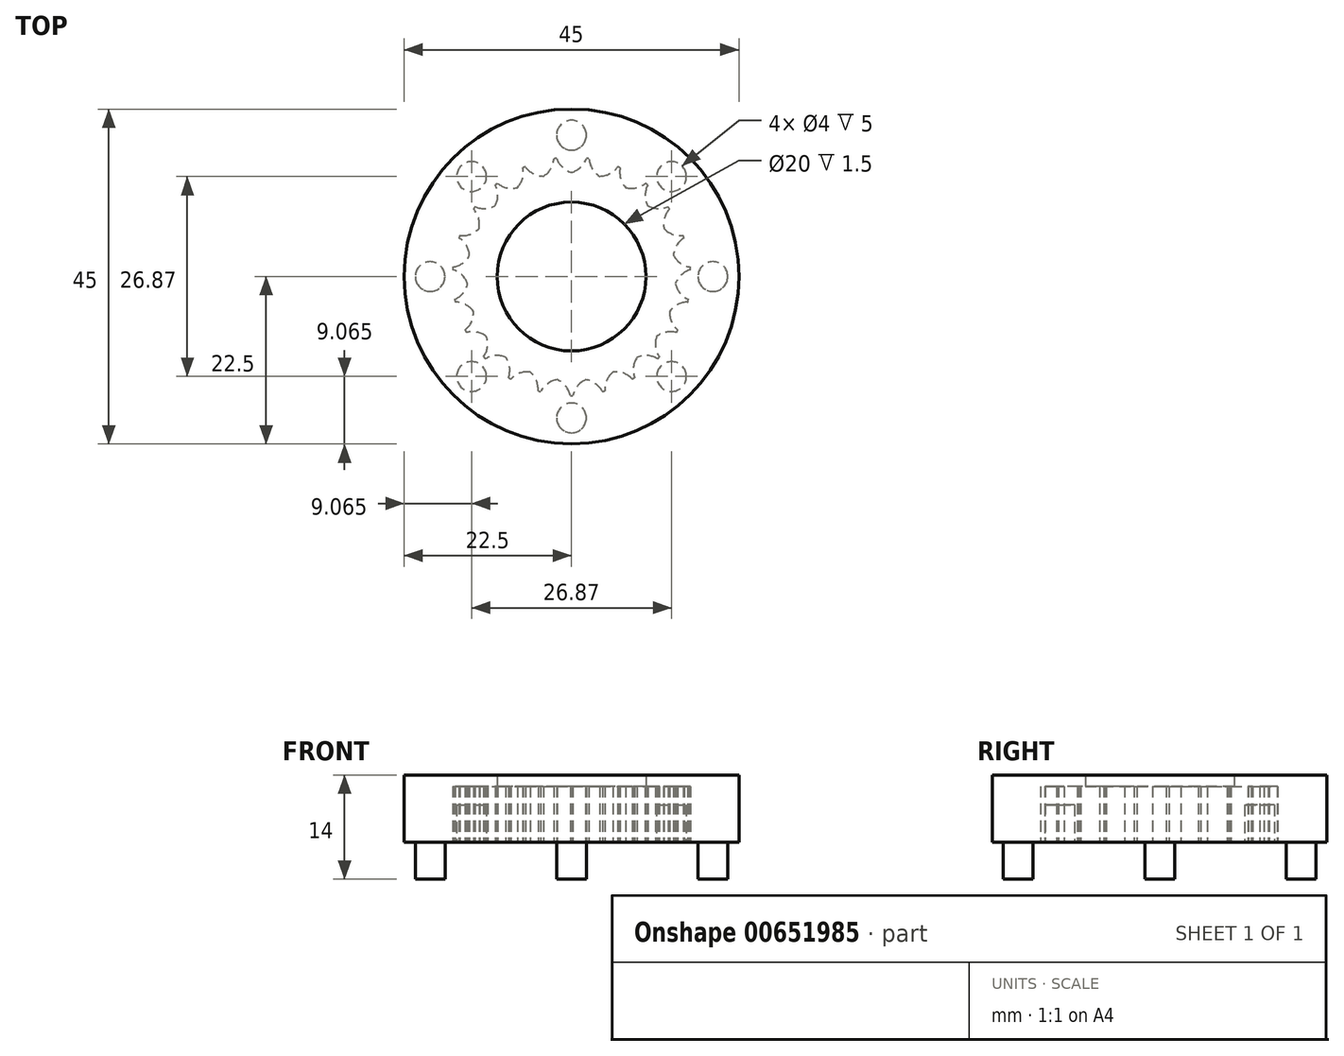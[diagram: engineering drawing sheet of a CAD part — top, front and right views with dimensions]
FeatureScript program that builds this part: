
annotation { "Feature Type Name" : "Feature", "Feature Type Description" : "" }
export const myFeature = defineFeature(function(context is Context, id is Id, definition is map)
    precondition{}
    {
        {
            var Q0;
            Q0=qCreatedBy(makeId("Top.planeOp"),FACE);
            var sketch = newSketch(context, id + "F0", { "sketchPlane" : qUnion([Q0])});
            skCircle(sketch, "E0", {"center": v(0, 0) * mm, "radius": 16 * mm});
            skCircle(sketch, "E1", {"center": v(0, 0) * mm, "radius": 22.5 * mm});
            skArc(sketch, "E2", {"start": v(-2, 15.87) * mm, "mid": v(-1.23, 14.7) * mm, "end": v(0, 14) * mm});
            skArc(sketch, "E3", {"start": v(0, 14) * mm, "mid": v(1.23, 14.7) * mm, "end": v(2, 15.87) * mm});
            skArc(sketch, "E4.1.0", {"start": v(-6.2, 14.75) * mm, "mid": v(-5.15, 13.82) * mm, "end": v(-3.78, 13.48) * mm});
            skArc(sketch, "E4.1.1", {"start": v(-3.78, 13.48) * mm, "mid": v(-2.78, 14.48) * mm, "end": v(-2.36, 15.83) * mm});
            skArc(sketch, "E4.2.0", {"start": v(-9.96, 12.52) * mm, "mid": v(-8.68, 11.92) * mm, "end": v(-7.27, 11.96) * mm});
            skArc(sketch, "E4.2.1", {"start": v(-7.27, 11.96) * mm, "mid": v(-6.59, 13.2) * mm, "end": v(-6.54, 14.6) * mm});
            skArc(sketch, "E4.3.0", {"start": v(-12.97, 9.37) * mm, "mid": v(-11.58, 9.13) * mm, "end": v(-10.23, 9.56) * mm});
            skArc(sketch, "E4.3.1", {"start": v(-10.23, 9.56) * mm, "mid": v(-9.9, 10.93) * mm, "end": v(-10.24, 12.3) * mm});
            skArc(sketch, "E4.4.0", {"start": v(-15.01, 5.53) * mm, "mid": v(-13.61, 5.67) * mm, "end": v(-12.43, 6.44) * mm});
            skArc(sketch, "E4.4.1", {"start": v(-12.43, 6.44) * mm, "mid": v(-12.48, 7.85) * mm, "end": v(-13.17, 9.08) * mm});
            skArc(sketch, "E4.5.0", {"start": v(-15.95, 1.27) * mm, "mid": v(-14.64, 1.79) * mm, "end": v(-13.7, 2.85) * mm});
            skArc(sketch, "E4.5.1", {"start": v(-13.7, 2.85) * mm, "mid": v(-14.14, 4.2) * mm, "end": v(-15.14, 5.19) * mm});
            skArc(sketch, "E4.6.0", {"start": v(-15.7, -3.08) * mm, "mid": v(-14.58, -2.23) * mm, "end": v(-13.97, -0.96) * mm});
            skArc(sketch, "E4.6.1", {"start": v(-13.97, -0.96) * mm, "mid": v(-14.74, 0.22) * mm, "end": v(-15.97, 0.91) * mm});
            skArc(sketch, "E4.7.0", {"start": v(-14.29, -7.2) * mm, "mid": v(-13.44, -6.08) * mm, "end": v(-13.2, -4.69) * mm});
            skArc(sketch, "E4.7.1", {"start": v(-13.2, -4.69) * mm, "mid": v(-14.26, -3.77) * mm, "end": v(-15.63, -3.43) * mm});
            skArc(sketch, "E4.8.0", {"start": v(-11.82, -10.79) * mm, "mid": v(-11.3, -9.48) * mm, "end": v(-11.44, -8.07) * mm});
            skArc(sketch, "E4.8.1", {"start": v(-11.44, -8.07) * mm, "mid": v(-12.71, -7.47) * mm, "end": v(-14.12, -7.52) * mm});
            skArc(sketch, "E4.9.0", {"start": v(-8.47, -13.58) * mm, "mid": v(-8.32, -12.17) * mm, "end": v(-8.84, -10.86) * mm});
            skArc(sketch, "E4.9.1", {"start": v(-8.84, -10.86) * mm, "mid": v(-10.23, -10.63) * mm, "end": v(-11.57, -11.05) * mm});
            skArc(sketch, "E4.10.0", {"start": v(-4.49, -15.36) * mm, "mid": v(-4.73, -13.97) * mm, "end": v(-5.58, -12.84) * mm});
            skArc(sketch, "E4.10.1", {"start": v(-5.58, -12.84) * mm, "mid": v(-6.98, -13) * mm, "end": v(-8.16, -13.76) * mm});
            skArc(sketch, "E4.11.0", {"start": v(-0.18, -16) * mm, "mid": v(-0.79, -14.73) * mm, "end": v(-1.9, -13.87) * mm});
            skArc(sketch, "E4.11.1", {"start": v(-1.9, -13.87) * mm, "mid": v(-3.22, -14.4) * mm, "end": v(-4.14, -15.45) * mm});
            skArc(sketch, "E4.12.0", {"start": v(4.14, -15.45) * mm, "mid": v(3.22, -14.4) * mm, "end": v(1.9, -13.87) * mm});
            skArc(sketch, "E4.12.1", {"start": v(1.9, -13.87) * mm, "mid": v(0.79, -14.73) * mm, "end": v(0.18, -16) * mm});
            skArc(sketch, "E4.13.0", {"start": v(8.16, -13.76) * mm, "mid": v(6.98, -13) * mm, "end": v(5.58, -12.84) * mm});
            skArc(sketch, "E4.13.1", {"start": v(5.58, -12.84) * mm, "mid": v(4.73, -13.97) * mm, "end": v(4.49, -15.36) * mm});
            skArc(sketch, "E4.14.0", {"start": v(11.57, -11.05) * mm, "mid": v(10.23, -10.63) * mm, "end": v(8.84, -10.86) * mm});
            skArc(sketch, "E4.14.1", {"start": v(8.84, -10.86) * mm, "mid": v(8.32, -12.17) * mm, "end": v(8.47, -13.58) * mm});
            skArc(sketch, "E4.15.0", {"start": v(14.12, -7.52) * mm, "mid": v(12.71, -7.47) * mm, "end": v(11.44, -8.07) * mm});
            skArc(sketch, "E4.15.1", {"start": v(11.44, -8.07) * mm, "mid": v(11.3, -9.48) * mm, "end": v(11.82, -10.79) * mm});
            skArc(sketch, "E4.16.0", {"start": v(15.63, -3.43) * mm, "mid": v(14.26, -3.77) * mm, "end": v(13.2, -4.69) * mm});
            skArc(sketch, "E4.16.1", {"start": v(13.2, -4.69) * mm, "mid": v(13.44, -6.08) * mm, "end": v(14.29, -7.2) * mm});
            skArc(sketch, "E4.17.0", {"start": v(15.97, 0.91) * mm, "mid": v(14.74, 0.22) * mm, "end": v(13.97, -0.96) * mm});
            skArc(sketch, "E4.17.1", {"start": v(13.97, -0.96) * mm, "mid": v(14.58, -2.23) * mm, "end": v(15.7, -3.08) * mm});
            skArc(sketch, "E4.18.0", {"start": v(15.14, 5.19) * mm, "mid": v(14.14, 4.2) * mm, "end": v(13.7, 2.85) * mm});
            skArc(sketch, "E4.18.1", {"start": v(13.7, 2.85) * mm, "mid": v(14.64, 1.79) * mm, "end": v(15.95, 1.27) * mm});
            skArc(sketch, "E4.19.0", {"start": v(13.17, 9.08) * mm, "mid": v(12.48, 7.85) * mm, "end": v(12.43, 6.44) * mm});
            skArc(sketch, "E4.19.1", {"start": v(12.43, 6.44) * mm, "mid": v(13.61, 5.67) * mm, "end": v(15.01, 5.53) * mm});
            skArc(sketch, "E4.20.0", {"start": v(10.24, 12.3) * mm, "mid": v(9.9, 10.93) * mm, "end": v(10.23, 9.56) * mm});
            skArc(sketch, "E4.20.1", {"start": v(10.23, 9.56) * mm, "mid": v(11.58, 9.13) * mm, "end": v(12.97, 9.37) * mm});
            skArc(sketch, "E4.21.0", {"start": v(6.54, 14.6) * mm, "mid": v(6.59, 13.2) * mm, "end": v(7.27, 11.96) * mm});
            skArc(sketch, "E4.21.1", {"start": v(7.27, 11.96) * mm, "mid": v(8.68, 11.92) * mm, "end": v(9.96, 12.52) * mm});
            skArc(sketch, "E4.22.0", {"start": v(2.36, 15.83) * mm, "mid": v(2.78, 14.48) * mm, "end": v(3.78, 13.48) * mm});
            skArc(sketch, "E4.22.1", {"start": v(3.78, 13.48) * mm, "mid": v(5.15, 13.82) * mm, "end": v(6.2, 14.75) * mm});
            skSolve(sketch);
        }
        {
            var Q0;
            Q0=makeQuery(id+"F0.imprint","IMPRINT",FACE,{"disambiguationData":[TD([[makeQuery(id+"F0.imprint","IMPRINT",EDGE,{"derivedFrom":sQuery(id+"F0.wireOp",EDGE,"E1")}),1.0]])]});
            var Q1;
            {var subQ0=sQuery(id+"F0.wireOp",EDGE,"E2");Q1=makeQuery(id+"F0.imprint","IMPRINT",FACE,{"disambiguationData":[TD([[makeQuery(id+"F0.imprint","IMPRINT",EDGE,{"derivedFrom":subQ0}),1.0]])]});}
            var Q2;
            {var subQ0=sQuery(id+"F0.wireOp",EDGE,"E4.1.0");Q2=makeQuery(id+"F0.imprint","IMPRINT",FACE,{"disambiguationData":[TD([[makeQuery(id+"F0.imprint","IMPRINT",EDGE,{"derivedFrom":subQ0}),1.0]])]});}
            var Q3;
            {var subQ0=sQuery(id+"F0.wireOp",EDGE,"E4.2.0");Q3=makeQuery(id+"F0.imprint","IMPRINT",FACE,{"disambiguationData":[TD([[makeQuery(id+"F0.imprint","IMPRINT",EDGE,{"derivedFrom":subQ0}),1.0]])]});}
            var Q4;
            {var subQ0=sQuery(id+"F0.wireOp",EDGE,"E4.3.0");Q4=makeQuery(id+"F0.imprint","IMPRINT",FACE,{"disambiguationData":[TD([[makeQuery(id+"F0.imprint","IMPRINT",EDGE,{"derivedFrom":subQ0}),1.0]])]});}
            var Q5;
            {var subQ0=sQuery(id+"F0.wireOp",EDGE,"E4.4.0");Q5=makeQuery(id+"F0.imprint","IMPRINT",FACE,{"disambiguationData":[TD([[makeQuery(id+"F0.imprint","IMPRINT",EDGE,{"derivedFrom":subQ0}),1.0]])]});}
            var Q6;
            {var subQ0=sQuery(id+"F0.wireOp",EDGE,"E4.5.0");Q6=makeQuery(id+"F0.imprint","IMPRINT",FACE,{"disambiguationData":[TD([[makeQuery(id+"F0.imprint","IMPRINT",EDGE,{"derivedFrom":subQ0}),1.0]])]});}
            var Q7;
            {var subQ0=sQuery(id+"F0.wireOp",EDGE,"E4.6.0");Q7=makeQuery(id+"F0.imprint","IMPRINT",FACE,{"disambiguationData":[TD([[makeQuery(id+"F0.imprint","IMPRINT",EDGE,{"derivedFrom":subQ0}),1.0]])]});}
            var Q8;
            {var subQ0=sQuery(id+"F0.wireOp",EDGE,"E4.7.0");Q8=makeQuery(id+"F0.imprint","IMPRINT",FACE,{"disambiguationData":[TD([[makeQuery(id+"F0.imprint","IMPRINT",EDGE,{"derivedFrom":subQ0}),1.0]])]});}
            var Q9;
            {var subQ0=sQuery(id+"F0.wireOp",EDGE,"E4.8.0");Q9=makeQuery(id+"F0.imprint","IMPRINT",FACE,{"disambiguationData":[TD([[makeQuery(id+"F0.imprint","IMPRINT",EDGE,{"derivedFrom":subQ0}),1.0]])]});}
            var Q10;
            {var subQ0=sQuery(id+"F0.wireOp",EDGE,"E4.9.0");Q10=makeQuery(id+"F0.imprint","IMPRINT",FACE,{"disambiguationData":[TD([[makeQuery(id+"F0.imprint","IMPRINT",EDGE,{"derivedFrom":subQ0}),1.0]])]});}
            var Q11;
            {var subQ0=sQuery(id+"F0.wireOp",EDGE,"E4.10.0");Q11=makeQuery(id+"F0.imprint","IMPRINT",FACE,{"disambiguationData":[TD([[makeQuery(id+"F0.imprint","IMPRINT",EDGE,{"derivedFrom":subQ0}),1.0]])]});}
            var Q12;
            {var subQ0=sQuery(id+"F0.wireOp",EDGE,"E4.11.0");Q12=makeQuery(id+"F0.imprint","IMPRINT",FACE,{"disambiguationData":[TD([[makeQuery(id+"F0.imprint","IMPRINT",EDGE,{"derivedFrom":subQ0}),1.0]])]});}
            var Q13;
            {var subQ0=sQuery(id+"F0.wireOp",EDGE,"E4.12.0");Q13=makeQuery(id+"F0.imprint","IMPRINT",FACE,{"disambiguationData":[TD([[makeQuery(id+"F0.imprint","IMPRINT",EDGE,{"derivedFrom":subQ0}),1.0]])]});}
            var Q14;
            {var subQ0=sQuery(id+"F0.wireOp",EDGE,"E4.13.0");Q14=makeQuery(id+"F0.imprint","IMPRINT",FACE,{"disambiguationData":[TD([[makeQuery(id+"F0.imprint","IMPRINT",EDGE,{"derivedFrom":subQ0}),1.0]])]});}
            var Q15;
            {var subQ0=sQuery(id+"F0.wireOp",EDGE,"E4.14.0");Q15=makeQuery(id+"F0.imprint","IMPRINT",FACE,{"disambiguationData":[TD([[makeQuery(id+"F0.imprint","IMPRINT",EDGE,{"derivedFrom":subQ0}),1.0]])]});}
            var Q16;
            {var subQ0=sQuery(id+"F0.wireOp",EDGE,"E4.15.0");Q16=makeQuery(id+"F0.imprint","IMPRINT",FACE,{"disambiguationData":[TD([[makeQuery(id+"F0.imprint","IMPRINT",EDGE,{"derivedFrom":subQ0}),1.0]])]});}
            var Q17;
            {var subQ0=sQuery(id+"F0.wireOp",EDGE,"E4.16.0");Q17=makeQuery(id+"F0.imprint","IMPRINT",FACE,{"disambiguationData":[TD([[makeQuery(id+"F0.imprint","IMPRINT",EDGE,{"derivedFrom":subQ0}),1.0]])]});}
            var Q18;
            {var subQ0=sQuery(id+"F0.wireOp",EDGE,"E4.17.0");Q18=makeQuery(id+"F0.imprint","IMPRINT",FACE,{"disambiguationData":[TD([[makeQuery(id+"F0.imprint","IMPRINT",EDGE,{"derivedFrom":subQ0}),1.0]])]});}
            var Q19;
            {var subQ0=sQuery(id+"F0.wireOp",EDGE,"E4.18.0");Q19=makeQuery(id+"F0.imprint","IMPRINT",FACE,{"disambiguationData":[TD([[makeQuery(id+"F0.imprint","IMPRINT",EDGE,{"derivedFrom":subQ0}),1.0]])]});}
            var Q20;
            {var subQ0=sQuery(id+"F0.wireOp",EDGE,"E4.19.0");Q20=makeQuery(id+"F0.imprint","IMPRINT",FACE,{"disambiguationData":[TD([[makeQuery(id+"F0.imprint","IMPRINT",EDGE,{"derivedFrom":subQ0}),1.0]])]});}
            var Q21;
            {var subQ0=sQuery(id+"F0.wireOp",EDGE,"E4.20.0");Q21=makeQuery(id+"F0.imprint","IMPRINT",FACE,{"disambiguationData":[TD([[makeQuery(id+"F0.imprint","IMPRINT",EDGE,{"derivedFrom":subQ0}),1.0]])]});}
            var Q22;
            {var subQ0=sQuery(id+"F0.wireOp",EDGE,"E4.21.0");Q22=makeQuery(id+"F0.imprint","IMPRINT",FACE,{"disambiguationData":[TD([[makeQuery(id+"F0.imprint","IMPRINT",EDGE,{"derivedFrom":subQ0}),1.0]])]});}
            var Q23;
            {var subQ0=sQuery(id+"F0.wireOp",EDGE,"E4.22.0");Q23=makeQuery(id+"F0.imprint","IMPRINT",FACE,{"disambiguationData":[TD([[makeQuery(id+"F0.imprint","IMPRINT",EDGE,{"derivedFrom":subQ0}),1.0]])]});}
            extrude(context, id + "F1", {"entities" : qUnion([Q0, Q1, Q2, Q3, Q4, Q5, Q6, Q7, Q8, Q9, Q10, Q11, Q12, Q13, Q14, Q15, Q16, Q17, Q18, Q19, Q20, Q21, Q22, Q23]), "depth" : 7.5 * mm, "offsetDistance" : 25 * mm});
        }
        {
            var Q0;
            Q0=makeQuery(id+"F1.opExtrude","CAP_FACE",FACE,{"disambiguationData":[OSD([sQuery(id+"F0.wireOp",EDGE,"E0"),sQuery(id+"F0.wireOp",EDGE,"E1"),sQuery(id+"F0.wireOp",EDGE,"E2"),sQuery(id+"F0.wireOp",EDGE,"E3"),sQuery(id+"F0.wireOp",EDGE,"E4.1.0"),sQuery(id+"F0.wireOp",EDGE,"E4.1.1"),sQuery(id+"F0.wireOp",EDGE,"E4.2.0"),sQuery(id+"F0.wireOp",EDGE,"E4.2.1"),sQuery(id+"F0.wireOp",EDGE,"E4.3.0"),sQuery(id+"F0.wireOp",EDGE,"E4.3.1"),sQuery(id+"F0.wireOp",EDGE,"E4.4.0"),sQuery(id+"F0.wireOp",EDGE,"E4.4.1"),sQuery(id+"F0.wireOp",EDGE,"E4.5.0"),sQuery(id+"F0.wireOp",EDGE,"E4.5.1"),sQuery(id+"F0.wireOp",EDGE,"E4.6.0"),sQuery(id+"F0.wireOp",EDGE,"E4.6.1"),sQuery(id+"F0.wireOp",EDGE,"E4.7.0"),sQuery(id+"F0.wireOp",EDGE,"E4.7.1"),sQuery(id+"F0.wireOp",EDGE,"E4.8.0"),sQuery(id+"F0.wireOp",EDGE,"E4.8.1"),sQuery(id+"F0.wireOp",EDGE,"E4.9.0"),sQuery(id+"F0.wireOp",EDGE,"E4.9.1"),sQuery(id+"F0.wireOp",EDGE,"E4.10.0"),sQuery(id+"F0.wireOp",EDGE,"E4.10.1"),sQuery(id+"F0.wireOp",EDGE,"E4.11.0"),sQuery(id+"F0.wireOp",EDGE,"E4.11.1"),sQuery(id+"F0.wireOp",EDGE,"E4.12.0"),sQuery(id+"F0.wireOp",EDGE,"E4.12.1"),sQuery(id+"F0.wireOp",EDGE,"E4.13.0"),sQuery(id+"F0.wireOp",EDGE,"E4.13.1"),sQuery(id+"F0.wireOp",EDGE,"E4.14.0"),sQuery(id+"F0.wireOp",EDGE,"E4.14.1"),sQuery(id+"F0.wireOp",EDGE,"E4.15.0"),sQuery(id+"F0.wireOp",EDGE,"E4.15.1"),sQuery(id+"F0.wireOp",EDGE,"E4.16.0"),sQuery(id+"F0.wireOp",EDGE,"E4.16.1"),sQuery(id+"F0.wireOp",EDGE,"E4.17.0"),sQuery(id+"F0.wireOp",EDGE,"E4.17.1"),sQuery(id+"F0.wireOp",EDGE,"E4.18.0"),sQuery(id+"F0.wireOp",EDGE,"E4.18.1"),sQuery(id+"F0.wireOp",EDGE,"E4.19.0"),sQuery(id+"F0.wireOp",EDGE,"E4.19.1"),sQuery(id+"F0.wireOp",EDGE,"E4.20.0"),sQuery(id+"F0.wireOp",EDGE,"E4.20.1"),sQuery(id+"F0.wireOp",EDGE,"E4.21.0"),sQuery(id+"F0.wireOp",EDGE,"E4.21.1"),sQuery(id+"F0.wireOp",EDGE,"E4.22.0"),sQuery(id+"F0.wireOp",EDGE,"E4.22.1")])],"isStart":true});
            var sketch = newSketch(context, id + "F2", { "sketchPlane" : qUnion([Q0])});
            skCircle(sketch, "E5", {"center": v(0, 19) * mm, "radius": 2 * mm});
            skCircle(sketch, "E6.1.0", {"center": v(-13.44, 13.44) * mm, "radius": 2 * mm});
            skCircle(sketch, "E6.2.0", {"center": v(-19, 0) * mm, "radius": 2 * mm});
            skCircle(sketch, "E6.3.0", {"center": v(-13.44, -13.44) * mm, "radius": 2 * mm});
            skCircle(sketch, "E6.4.0", {"center": v(0, -19) * mm, "radius": 2 * mm});
            skCircle(sketch, "E6.5.0", {"center": v(13.44, -13.44) * mm, "radius": 2 * mm});
            skCircle(sketch, "E6.6.0", {"center": v(19, 0) * mm, "radius": 2 * mm});
            skCircle(sketch, "E6.7.0", {"center": v(13.44, 13.44) * mm, "radius": 2 * mm});
            skPoint(sketch, "E6.center", {"position": v(0, 0) * mm});
            skSolve(sketch);
        }
        {
            var Q0;
            Q0=makeQuery(id+"F2.imprint","IMPRINT",FACE,{"disambiguationData":[TD([[makeQuery(id+"F2.imprint","IMPRINT",EDGE,{"derivedFrom":sQuery(id+"F2.wireOp",EDGE,"E5")}),1.0]])]});
            var Q1;
            Q1=makeQuery(id+"F2.imprint","IMPRINT",FACE,{"disambiguationData":[TD([[makeQuery(id+"F2.imprint","IMPRINT",EDGE,{"derivedFrom":sQuery(id+"F2.wireOp",EDGE,"E6.2.0")}),1.0]])]});
            var Q2;
            Q2=makeQuery(id+"F2.imprint","IMPRINT",FACE,{"disambiguationData":[TD([[makeQuery(id+"F2.imprint","IMPRINT",EDGE,{"derivedFrom":sQuery(id+"F2.wireOp",EDGE,"E6.6.0")}),1.0]])]});
            var Q3;
            Q3=makeQuery(id+"F2.imprint","IMPRINT",FACE,{"disambiguationData":[TD([[makeQuery(id+"F2.imprint","IMPRINT",EDGE,{"derivedFrom":sQuery(id+"F2.wireOp",EDGE,"E6.4.0")}),1.0]])]});
            extrude(context, id + "F3", {"entities" : qUnion([Q0, Q1, Q2, Q3]), "operationType" : NewBodyOperationType.ADD, "depth" : 5 * mm, "offsetDistance" : 25 * mm});
        }
        {
            var Q0;
            Q0=makeQuery(id+"F2.imprint","IMPRINT",FACE,{"disambiguationData":[TD([[makeQuery(id+"F2.imprint","IMPRINT",EDGE,{"derivedFrom":sQuery(id+"F2.wireOp",EDGE,"E6.1.0")}),1.0]])]});
            var Q1;
            Q1=makeQuery(id+"F2.imprint","IMPRINT",FACE,{"disambiguationData":[TD([[makeQuery(id+"F2.imprint","IMPRINT",EDGE,{"derivedFrom":sQuery(id+"F2.wireOp",EDGE,"E6.7.0")}),1.0]])]});
            var Q2;
            Q2=makeQuery(id+"F2.imprint","IMPRINT",FACE,{"disambiguationData":[TD([[makeQuery(id+"F2.imprint","IMPRINT",EDGE,{"derivedFrom":sQuery(id+"F2.wireOp",EDGE,"E6.3.0")}),1.0]])]});
            var Q3;
            Q3=makeQuery(id+"F2.imprint","IMPRINT",FACE,{"disambiguationData":[TD([[makeQuery(id+"F2.imprint","IMPRINT",EDGE,{"derivedFrom":sQuery(id+"F2.wireOp",EDGE,"E6.5.0")}),1.0]])]});
            extrude(context, id + "F4", {"entities" : qUnion([Q0, Q1, Q2, Q3]), "operationType" : NewBodyOperationType.REMOVE, "oppositeDirection" : true, "depth" : 5 * mm, "offsetDistance" : 25 * mm});
        }
        {
            var Q0;
            Q0=makeQuery(id+"F1.opExtrude","CAP_FACE",FACE,{"disambiguationData":[OSD([sQuery(id+"F0.wireOp",EDGE,"E0"),sQuery(id+"F0.wireOp",EDGE,"E1"),sQuery(id+"F0.wireOp",EDGE,"E2"),sQuery(id+"F0.wireOp",EDGE,"E3"),sQuery(id+"F0.wireOp",EDGE,"E4.1.0"),sQuery(id+"F0.wireOp",EDGE,"E4.1.1"),sQuery(id+"F0.wireOp",EDGE,"E4.2.0"),sQuery(id+"F0.wireOp",EDGE,"E4.2.1"),sQuery(id+"F0.wireOp",EDGE,"E4.3.0"),sQuery(id+"F0.wireOp",EDGE,"E4.3.1"),sQuery(id+"F0.wireOp",EDGE,"E4.4.0"),sQuery(id+"F0.wireOp",EDGE,"E4.4.1"),sQuery(id+"F0.wireOp",EDGE,"E4.5.0"),sQuery(id+"F0.wireOp",EDGE,"E4.5.1"),sQuery(id+"F0.wireOp",EDGE,"E4.6.0"),sQuery(id+"F0.wireOp",EDGE,"E4.6.1"),sQuery(id+"F0.wireOp",EDGE,"E4.7.0"),sQuery(id+"F0.wireOp",EDGE,"E4.7.1"),sQuery(id+"F0.wireOp",EDGE,"E4.8.0"),sQuery(id+"F0.wireOp",EDGE,"E4.8.1"),sQuery(id+"F0.wireOp",EDGE,"E4.9.0"),sQuery(id+"F0.wireOp",EDGE,"E4.9.1"),sQuery(id+"F0.wireOp",EDGE,"E4.10.0"),sQuery(id+"F0.wireOp",EDGE,"E4.10.1"),sQuery(id+"F0.wireOp",EDGE,"E4.11.0"),sQuery(id+"F0.wireOp",EDGE,"E4.11.1"),sQuery(id+"F0.wireOp",EDGE,"E4.12.0"),sQuery(id+"F0.wireOp",EDGE,"E4.12.1"),sQuery(id+"F0.wireOp",EDGE,"E4.13.0"),sQuery(id+"F0.wireOp",EDGE,"E4.13.1"),sQuery(id+"F0.wireOp",EDGE,"E4.14.0"),sQuery(id+"F0.wireOp",EDGE,"E4.14.1"),sQuery(id+"F0.wireOp",EDGE,"E4.15.0"),sQuery(id+"F0.wireOp",EDGE,"E4.15.1"),sQuery(id+"F0.wireOp",EDGE,"E4.16.0"),sQuery(id+"F0.wireOp",EDGE,"E4.16.1"),sQuery(id+"F0.wireOp",EDGE,"E4.17.0"),sQuery(id+"F0.wireOp",EDGE,"E4.17.1"),sQuery(id+"F0.wireOp",EDGE,"E4.18.0"),sQuery(id+"F0.wireOp",EDGE,"E4.18.1"),sQuery(id+"F0.wireOp",EDGE,"E4.19.0"),sQuery(id+"F0.wireOp",EDGE,"E4.19.1"),sQuery(id+"F0.wireOp",EDGE,"E4.20.0"),sQuery(id+"F0.wireOp",EDGE,"E4.20.1"),sQuery(id+"F0.wireOp",EDGE,"E4.21.0"),sQuery(id+"F0.wireOp",EDGE,"E4.21.1"),sQuery(id+"F0.wireOp",EDGE,"E4.22.0"),sQuery(id+"F0.wireOp",EDGE,"E4.22.1")])],"isStart":false});
            var sketch = newSketch(context, id + "F5", { "sketchPlane" : qUnion([Q0])});
            skCircle(sketch, "E7", {"center": v(0, 0) * mm, "radius": 22.5 * mm});
            skCircle(sketch, "E8", {"center": v(0, 0) * mm, "radius": 10 * mm});
            skSolve(sketch);
        }
        {
            var Q0;
            Q0=makeQuery(id+"F5.imprint","IMPRINT",FACE,{"disambiguationData":[TD([[makeQuery(id+"F5.imprint","IMPRINT",EDGE,{"derivedFrom":sQuery(id+"F5.wireOp",EDGE,"E8")}),-1.0]])]});
            var Q1;
            Q1=makeQuery(id+"F5.imprint","IMPRINT",FACE,{"disambiguationData":[TD([[makeQuery(id+"F5.imprint","IMPRINT",EDGE,{"derivedFrom":sQuery(id+"F5.wireOp",EDGE,"E7")}),1.0]])]});
            extrude(context, id + "F6", {"entities" : qUnion([Q0, Q1]), "operationType" : NewBodyOperationType.ADD, "depth" : 1.5 * mm, "offsetDistance" : 25 * mm});
        }
    });
